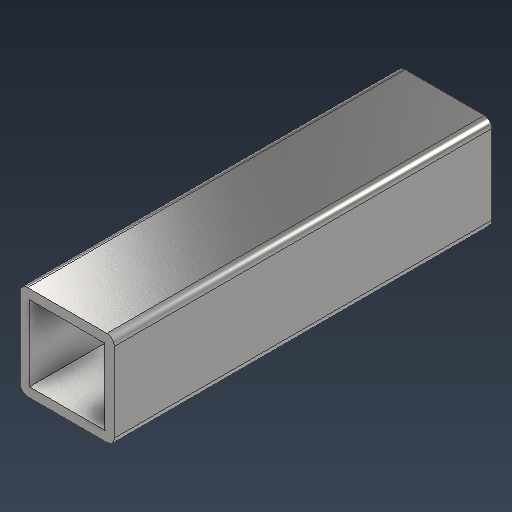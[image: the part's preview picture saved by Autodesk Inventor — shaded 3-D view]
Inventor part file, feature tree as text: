
AUTODESK INVENTOR PART (.ipt)
format: ipt  version: 2021 (Build 250183000, 183)  size: 187,392 bytes
history: native  units: mm
features: extrude x1, fillet x1, plane x1, split x1, other x1, sketch x1
ambient origin geometry x8: Origin, YZ Plane, XZ Plane, XY Plane, X Axis, Y Axis, Z Axis, Center Point
bodies: Solid1 (feature_tree)
feature tree (6):
  extrude  "Extrusion1"  Depth=25.0mm
  fillet  "Fillet1"  Radius=12.5mm
  plane  "Work Plane1"
  split  "Split1"
  other  "axialPlane"
  sketch  "Sketch1"  dims[d0=25.0mm d1=25.0mm d2=12.5mm d3=12.5mm d4=2.5mm d5=1000.0mm d6=0.0mm d7=2.0mm d8=-100.0mm]
